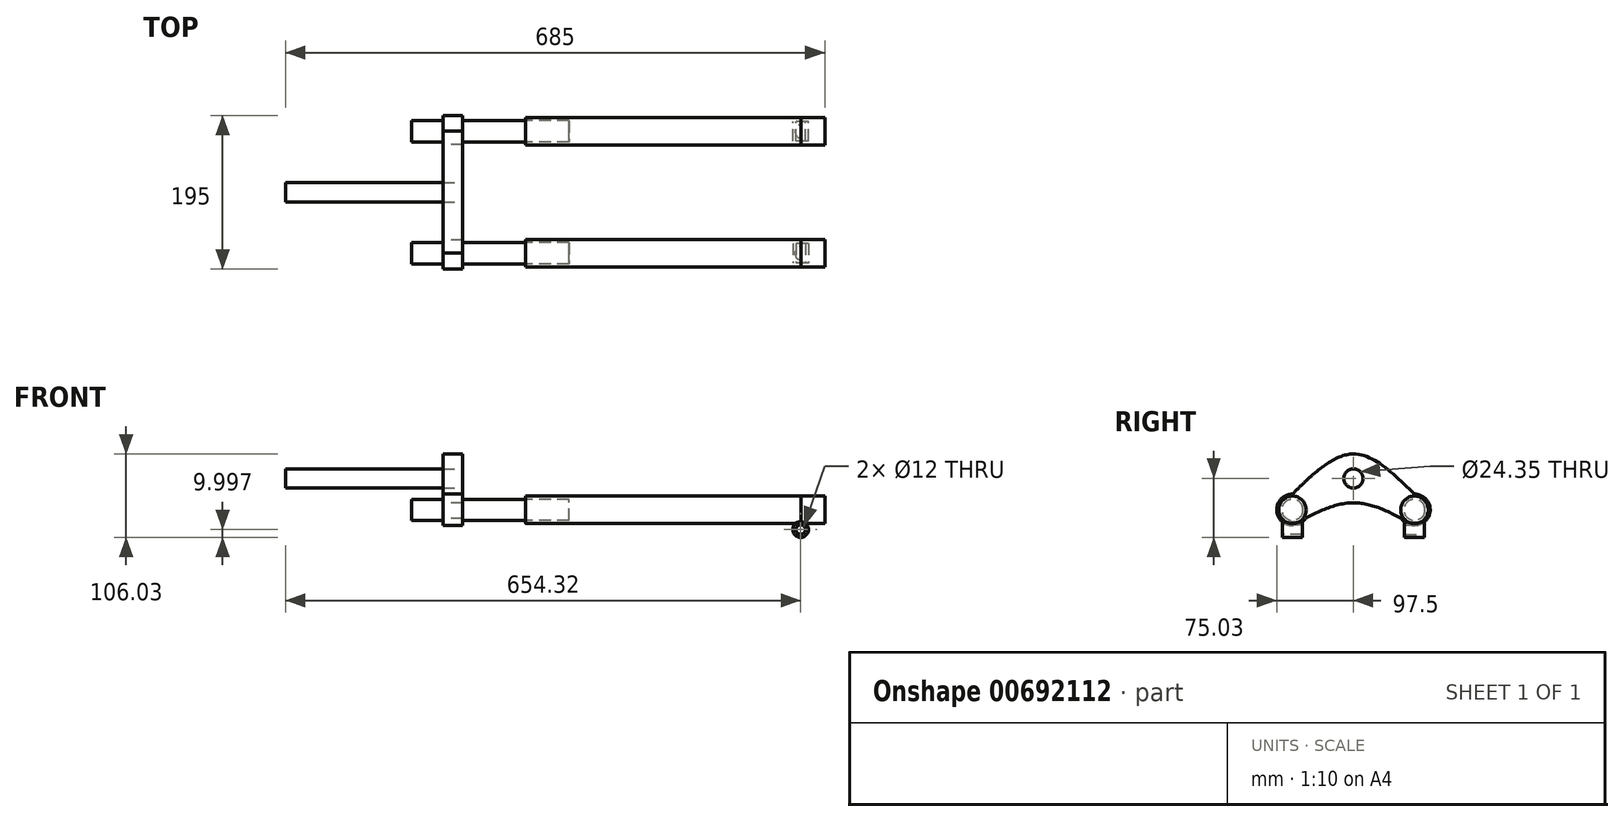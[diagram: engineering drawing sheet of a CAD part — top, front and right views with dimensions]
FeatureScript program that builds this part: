
annotation { "Feature Type Name" : "Feature", "Feature Type Description" : "" }
export const myFeature = defineFeature(function(context is Context, id is Id, definition is map)
    precondition{}
    {
        {
            var Q0;
            Q0=qCreatedBy(makeId("Right.planeOp"),FACE);
            var sketch = newSketch(context, id + "F0", { "sketchPlane" : qUnion([Q0])});
            skLineSegment(sketch, "E0", {"start": v(0, 0) * mm, "end": v(-77.5, 0) * mm, "construction": true});
            skLineSegment(sketch, "E1", {"start": v(0, 0) * mm, "end": v(77.5, 0) * mm, "construction": true});
            skLineSegment(sketch, "E2.0", {"start": v(0, 40) * mm, "end": v(77.5, 40) * mm, "construction": true});
            skLineSegment(sketch, "E2.1", {"start": v(0, 40) * mm, "end": v(-77.5, 40) * mm, "construction": true});
            skLineSegment(sketch, "E3", {"start": v(0, 0) * mm, "end": v(0, 40) * mm, "construction": true});
            skLineSegment(sketch, "E4.0", {"start": v(77.5, 0) * mm, "end": v(77.5, 40) * mm, "construction": true});
            skLineSegment(sketch, "E5.0", {"start": v(-77.5, 0) * mm, "end": v(-77.5, 40) * mm, "construction": true});
            skCircle(sketch, "E6", {"center": v(-77.5, 0) * mm, "radius": 13.5 * mm});
            skCircle(sketch, "E7", {"center": v(77.5, 0) * mm, "radius": 13.5 * mm});
            skCircle(sketch, "E8", {"center": v(77.5, 0) * mm, "radius": 20 * mm});
            skCircle(sketch, "E9", {"center": v(-77.5, 0) * mm, "radius": 20 * mm});
            skCircle(sketch, "E10", {"center": v(0, 40) * mm, "radius": 12.18 * mm});
            skCircle(sketch, "E11", {"center": v(0, 40) * mm, "radius": 31 * mm});
            skLineSegment(sketch, "E12.MirrorCS", {"start": v(77.5, 0) * mm, "end": v(77.5, -40) * mm, "construction": true});
            skLineSegment(sketch, "E13.MirrorCS", {"start": v(-77.5, 0) * mm, "end": v(-77.5, -40) * mm, "construction": true});
            skLineSegment(sketch, "E14.0", {"start": v(5, 45) * mm, "end": v(-77.5, 45) * mm});
            skLineSegment(sketch, "E14.1", {"start": v(5, 0) * mm, "end": v(5, 45) * mm});
            skLineSegment(sketch, "E15", {"start": v(0, 40) * mm, "end": v(0, 74.35) * mm, "construction": true});
            skPoint(sketch, "E16", {"position": v(0, 71) * mm});
            skPoint(sketch, "E17", {"position": v(77.5, 20) * mm});
            skPoint(sketch, "E18", {"position": v(-77.5, 20) * mm});
            skFitSpline(sketch, "E19", {"points": [v(77.5, 20) * mm, v(0, 71) * mm, v(-77.5, 20) * mm], "startDerivative": vector(-155, 153) * mm, "endDerivative": vector(-155, -153) * mm});
            skPoint(sketch, "E20", {"position": v(77.5, -20) * mm});
            skPoint(sketch, "E21", {"position": v(0, 9) * mm});
            skPoint(sketch, "E22", {"position": v(-77.5, -20) * mm});
            skFitSpline(sketch, "E23", {"points": [v(77.5, -20) * mm, v(0, 9) * mm, v(-77.5, -20) * mm], "startDerivative": vector(-155, 87) * mm, "endDerivative": vector(-155, -87) * mm});
            skSolve(sketch);
        }
        {
            var Q0;
            Q0=makeQuery(id+"F0.imprint","IMPRINT",FACE,{"disambiguationData":[TD([[makeQuery(id+"F0.imprint","IMPRINT",EDGE,{"derivedFrom":sQuery(id+"F0.wireOp",EDGE,"E7")}),1.0]])]});
            var Q1;
            Q1=makeQuery(id+"F0.imprint","IMPRINT",FACE,{"disambiguationData":[TD([[makeQuery(id+"F0.imprint","IMPRINT",EDGE,{"derivedFrom":sQuery(id+"F0.wireOp",EDGE,"E6")}),1.0]])]});
            extrude(context, id + "F1", {"entities" : qUnion([Q0, Q1]), "depth" : 160 * mm, "offsetDistance" : 25 * mm});
        }
        {
            var Q0;
            Q0=qSketchRegion(id+"F0",true);
            extrude(context, id + "F2", {"entities" : qUnion([Q0]), "depth" : 25 * mm, "offsetDistance" : 25 * mm});
        }
        {
            var Q0;
            Q0=makeQuery(id+"F1.opExtrude","CAP_FACE",FACE,{"disambiguationData":[OSD([sQuery(id+"F0.wireOp",EDGE,"E7")])],"isStart":false});
            var sketch = newSketch(context, id + "F3", { "sketchPlane" : qUnion([Q0])});
            skCircle(sketch, "E24", {"center": v(77.5, 0) * mm, "radius": 17.5 * mm});
            skSolve(sketch);
        }
        {
            var Q0;
            Q0=makeQuery(id+"F1.opExtrude","CAP_FACE",FACE,{"disambiguationData":[OSD([sQuery(id+"F0.wireOp",EDGE,"E6")])],"isStart":false});
            var sketch = newSketch(context, id + "F4", { "sketchPlane" : qUnion([Q0])});
            skCircle(sketch, "E25", {"center": v(-77.5, 0) * mm, "radius": 17.5 * mm});
            skSolve(sketch);
        }
        {
            var Q0;
            Q0=makeQuery(id+"F4.imprint","IMPRINT",FACE,{"disambiguationData":[TD([[makeQuery(id+"F4.imprint","IMPRINT",EDGE,{"derivedFrom":sQuery(id+"F4.wireOp",EDGE,"E25")}),1.0]])]});
            var Q1;
            Q1=makeQuery(id+"F3.imprint","IMPRINT",FACE,{"disambiguationData":[TD([[makeQuery(id+"F3.imprint","IMPRINT",EDGE,{"derivedFrom":sQuery(id+"F3.wireOp",EDGE,"E24")}),1.0]])]});
            var Q2;
            Q2=makeQuery(id+"F4.imprint","IMPRINT",FACE,{"disambiguationData":[TD([[makeQuery(id+"F4.imprint","IMPRINT",EDGE,{"derivedFrom":makeQuery(id+"F1.opExtrude","CAP_EDGE",EDGE,{"disambiguationData":[OSD([sQuery(id+"F0.wireOp",EDGE,"E6")])],"isStart":false})}),1.0]])]});
            var Q3;
            Q3=makeQuery(id+"F3.imprint","IMPRINT",FACE,{"disambiguationData":[TD([[makeQuery(id+"F3.imprint","IMPRINT",EDGE,{"derivedFrom":makeQuery(id+"F1.opExtrude","CAP_EDGE",EDGE,{"disambiguationData":[OSD([sQuery(id+"F0.wireOp",EDGE,"E7")])],"isStart":false})}),1.0]])]});
            extrude(context, id + "F5", {"entities" : qUnion([Q0, Q1, Q2, Q3]), "depth" : 295 * mm, "offsetDistance" : 25 * mm, "hasSecondDirection" : true, "secondDirectionOppositeDirection" : true, "secondDirectionDepth" : 55 * mm});
        }
        {
            var Q0;
            Q0=makeQuery(id+"F5.opExtrude","CAP_FACE",FACE,{"disambiguationData":[OSD([sQuery(id+"F4.wireOp",EDGE,"E25")])],"isStart":false});
            var sketch = newSketch(context, id + "F6", { "sketchPlane" : qUnion([Q0])});
            skLineSegment(sketch, "E26", {"start": v(109.4, 0) * mm, "end": v(-105.9, 0) * mm, "construction": true});
            skLineSegment(sketch, "E27.0", {"start": v(78.55, -17.5) * mm, "end": v(-77.5, -17.5) * mm, "construction": true});
            skArc(sketch, "E28.0", {"start": v(32.34, -46.42) * mm, "mid": v(132.3, -34.52) * mm, "end": v(99.87, 60.78) * mm, "construction": true});
            skFitSpline(sketch, "E28.1", {"points": [v(-55.59, -59.04) * mm, v(-52.36, -57.22) * mm, v(-46.07, -53.7) * mm, v(-37.18, -48.87) * mm, v(-28.88, -44.65) * mm, v(-21.25, -41.18) * mm, v(-15.56, -39) * mm, v(-11.47, -37.7) * mm, v(-8.66, -36.93) * mm, v(-6.1, -36.38) * mm, v(-4.19, -36.07) * mm, v(-2.79, -35.9) * mm, v(-1.8, -35.82) * mm, v(-1.02, -35.78) * mm, v(-0.43, -35.77) * mm, v(0, -35.76) * mm, v(0.43, -35.77) * mm, v(1.02, -35.78) * mm, v(1.8, -35.82) * mm, v(2.79, -35.9) * mm, v(4.19, -36.07) * mm, v(6.1, -36.38) * mm, v(8.66, -36.93) * mm, v(11.47, -37.7) * mm, v(15.56, -39) * mm, v(21.25, -41.18) * mm, v(28.88, -44.65) * mm, v(37.18, -48.87) * mm, v(46.07, -53.7) * mm, v(52.36, -57.22) * mm, v(55.59, -59.04) * mm], "construction": true});
            skArc(sketch, "E28.2", {"start": v(-99.87, 60.78) * mm, "mid": v(-132.3, -34.52) * mm, "end": v(-32.34, -46.42) * mm, "construction": true});
            skFitSpline(sketch, "E28.3", {"points": [v(108.95, 51.86) * mm, v(105.72, 55.05) * mm, v(99.1, 61.58) * mm, v(88.64, 71.6) * mm, v(77.54, 81.54) * mm, v(67.58, 89.55) * mm, v(59, 95.64) * mm, v(52.21, 100) * mm, v(44.97, 104.08) * mm, v(37.22, 107.8) * mm, v(30.27, 110.5) * mm, v(24.38, 112.32) * mm, v(19.8, 113.5) * mm, v(15.07, 114.47) * mm, v(11, 115.08) * mm, v(7.67, 115.43) * mm, v(5.14, 115.62) * mm, v(3.01, 115.72) * mm, v(1.3, 115.76) * mm, v(0, 115.77) * mm, v(-1.3, 115.76) * mm, v(-3.01, 115.72) * mm, v(-5.14, 115.62) * mm, v(-7.67, 115.43) * mm, v(-11, 115.08) * mm, v(-15.07, 114.47) * mm, v(-19.8, 113.5) * mm, v(-24.38, 112.32) * mm, v(-30.27, 110.5) * mm, v(-37.22, 107.8) * mm, v(-44.97, 104.08) * mm, v(-52.21, 100) * mm, v(-59, 95.64) * mm, v(-67.58, 89.55) * mm, v(-77.54, 81.54) * mm, v(-88.64, 71.6) * mm, v(-99.1, 61.58) * mm, v(-105.72, 55.05) * mm, v(-108.95, 51.86) * mm], "construction": true});
            skPoint(sketch, "E29.orphan", {"position": v(78.55, 0) * mm});
            skLineSegment(sketch, "E30.0", {"start": v(109.4, 30) * mm, "end": v(-105.9, 30) * mm, "construction": true});
            skSolve(sketch);
        }
        {
            var Q0;
            Q0=makeQuery(id+"F5.opExtrude","CAP_FACE",FACE,{"disambiguationData":[OSD([sQuery(id+"F3.wireOp",EDGE,"E24")])],"isStart":false});
            var sketch = newSketch(context, id + "F7", { "sketchPlane" : qUnion([Q0])});
            skCircle(sketch, "E31", {"center": v(77.5, 0) * mm, "radius": 25 * mm});
            skCircle(sketch, "E32", {"center": v(-77.43, 0) * mm, "radius": 25 * mm});
            skLineSegment(sketch, "E33", {"start": v(-77.43, 0) * mm, "end": v(-77.43, -25) * mm, "construction": true});
            skLineSegment(sketch, "E34", {"start": v(77.5, 0) * mm, "end": v(77.5, -25) * mm, "construction": true});
            skSolve(sketch);
        }
        {
            var Q0;
            Q0=sQuery(id+"F7.wireOp",EDGE,"E34");
            cPlane(context, id + "F8", {"entities" : qUnion([Q0]), "cplaneType" : CPlaneType.LINE_ANGLE, "offset" : 25 * mm, "angle" : 270 * degree, "width" : 150 * mm, "height" : 150 * mm});
        }
        {
            var Q0;
            Q0=qCreatedBy(id+"F8.planeOp",FACE);
            var sketch = newSketch(context, id + "F9", { "sketchPlane" : qUnion([Q0])});
            skCircle(sketch, "E35", {"center": v(454.32, -25.03) * mm, "radius": 6 * mm});
            skCircle(sketch, "E36", {"center": v(454.32, -25.03) * mm, "radius": 10 * mm});
            skSolve(sketch);
        }
        {
            var Q0;
            Q0=makeQuery(id+"F9.imprint","IMPRINT",FACE,{"disambiguationData":[TD([[makeQuery(id+"F9.imprint","IMPRINT",EDGE,{"derivedFrom":sQuery(id+"F9.wireOp",EDGE,"Bp49uNEs-YHsI-Nrd6-uTtH-Nd7ZtJ3mMyZP")}),-1.0]])]});
            var Q1;
            Q1=makeQuery(id+"F9.imprint","IMPRINT",FACE,{"disambiguationData":[TD([[makeQuery(id+"F9.imprint","IMPRINT",EDGE,{"derivedFrom":sQuery(id+"F9.wireOp",EDGE,"E35")}),-1.0]])]});
            extrude(context, id + "F10", {"entities" : qUnion([Q0, Q1]), "depth" : 12.5 * mm, "offsetDistance" : 25 * mm});
        }
        {
            var Q0;
            Q0=makeQuery(id+"F10.opExtrude","CAP_FACE",FACE,{"disambiguationData":[OSD([sQuery(id+"F9.wireOp",EDGE,"Bp49uNEs-YHsI-Nrd6-uTtH-Nd7ZtJ3mMyZP"),sQuery(id+"F9.wireOp",EDGE,"RS6dVKnX-jJ1k-Fsq9-aOxC-NDbp3NSvcxQR")])],"isStart":true});
            var Q1;
            Q1=makeQuery(id+"F10.opExtrude","CAP_FACE",FACE,{"disambiguationData":[OSD([sQuery(id+"F9.wireOp",EDGE,"E35"),sQuery(id+"F9.wireOp",EDGE,"E36")])],"isStart":true});
            extrude(context, id + "F11", {"entities" : qUnion([Q0, Q1]), "depth" : 12.5 * mm, "offsetDistance" : 25 * mm});
        }
        {
            var Q0;
            Q0=makeQuery(id+"F10.opExtrude","SWEPT_BODY",BODY,{"disambiguationData":[OSD([sQuery(id+"F9.wireOp",EDGE,"E35"),sQuery(id+"F9.wireOp",EDGE,"E36")])]});
            var Q1;
            Q1=makeQuery(id+"F11.opExtrude","SWEPT_BODY",BODY,{"disambiguationData":[OSD([sQuery(id+"F9.wireOp",EDGE,"E35"),sQuery(id+"F9.wireOp",EDGE,"E36")])]});
            var Q2;
            Q2=qCreatedBy(makeId("Front.planeOp"),FACE);
            mirror(context, id + "F12", {"operationType" : NewBodyOperationType.ADD, "entities" : qUnion([Q0, Q1]), "mirrorPlane" : qUnion([Q2])});
        }
        {
            var Q0;
            Q0=makeQuery(id+"F7.imprint","IMPRINT",FACE,{"disambiguationData":[TD([[makeQuery(id+"F7.imprint","IMPRINT",EDGE,{"derivedFrom":makeQuery(id+"F5.opExtrude","CAP_EDGE",EDGE,{"disambiguationData":[OSD([sQuery(id+"F3.wireOp",EDGE,"E24")])],"isStart":false})}),1.0]])]});
            var Q1;
            Q1=makeQuery(id+"F6.imprint","IMPRINT",FACE,{"disambiguationData":[TD([[makeQuery(id+"F6.imprint","IMPRINT",EDGE,{"derivedFrom":makeQuery(id+"F5.opExtrude","CAP_EDGE",EDGE,{"disambiguationData":[OSD([sQuery(id+"F4.wireOp",EDGE,"E25")])],"isStart":false})}),1.0]])]});
            extrude(context, id + "F13", {"entities" : qUnion([Q0, Q1]), "depth" : 30 * mm, "offsetDistance" : 25 * mm});
        }
        {
            var Q0;
            Q0=makeQuery(id+"F1.opExtrude","CAP_FACE",FACE,{"disambiguationData":[OSD([sQuery(id+"F0.wireOp",EDGE,"E7")])],"isStart":true});
            extrude(context, id + "F14", {"entities" : qUnion([Q0]), "operationType" : NewBodyOperationType.ADD, "depth" : 40 * mm, "offsetDistance" : 25 * mm});
        }
        {
            var Q0;
            Q0=makeQuery(id+"F1.opExtrude","CAP_FACE",FACE,{"disambiguationData":[OSD([sQuery(id+"F0.wireOp",EDGE,"E6")])],"isStart":true});
            extrude(context, id + "F15", {"entities" : qUnion([Q0]), "operationType" : NewBodyOperationType.ADD, "depth" : 40 * mm, "offsetDistance" : 25 * mm});
        }
        {
            var Q0;
            {var subQ0=sQuery(id+"F0.wireOp",EDGE,"E14.0");var subQ1=sQuery(id+"F0.wireOp",EDGE,"E10");var subQ2=makeQuery(id+"F0.imprint","INTERSECT",VERTEX,{"derivedFrom":[subQ1,subQ0]});Q0=makeQuery(id+"F0.imprint","IMPRINT",FACE,{"disambiguationData":[TD([[makeQuery(id+"F0.imprint","IMPRINT",EDGE,{"disambiguationData":[TD([[subQ2,1.0]])],"derivedFrom":subQ1}),1.0]])]});}
            var Q1;
            {var subQ0=sQuery(id+"F0.wireOp",EDGE,"E14.0");var subQ1=sQuery(id+"F0.wireOp",EDGE,"E10");var subQ2=makeQuery(id+"F0.imprint","INTERSECT",VERTEX,{"derivedFrom":[subQ1,subQ0]});Q1=makeQuery(id+"F0.imprint","IMPRINT",FACE,{"disambiguationData":[TD([[makeQuery(id+"F0.imprint","IMPRINT",EDGE,{"disambiguationData":[TD([[subQ2,-1.0]])],"derivedFrom":subQ1}),1.0]])]});}
            extrude(context, id + "F16", {"entities" : qUnion([Q0, Q1]), "oppositeDirection" : true, "depth" : 200 * mm, "offsetDistance" : 25 * mm, "hasSecondDirection" : true, "secondDirectionOppositeDirection" : false, "secondDirectionDepth" : 25 * mm});
        }
    });
